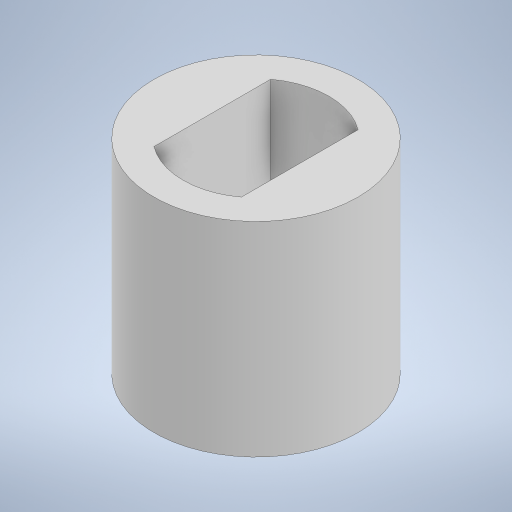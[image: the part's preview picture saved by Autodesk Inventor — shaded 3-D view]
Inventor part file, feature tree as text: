
AUTODESK INVENTOR PART (.ipt)
format: ipt  version: 2023 (Build 270158000, 158)  size: 248,320 bytes
history: native  units: in
note: dims shown in document units (in); Inventor stores cm internally (conversion verified against a paired STEP export)
features: extrude x2, sketch x2
ambient origin geometry x8: Origin, YZ Plane, XZ Plane, XY Plane, X Axis, Y Axis, Z Axis, Center Point
bodies: Solid1 (feature_tree)
feature tree (4):
  extrude  "Extrusion1"  Depth=0.2756in TaperAngle=0.0deg
  extrude  "Extrusion2"  Depth=0.1181in
  sketch  "Sketch1"  dims[d0=0.2756in d1=0.2756in d2=0.0in]
  sketch  "Sketch2"  dims[d3=0.1969in d4=0.1181in d5=0.2165in d6=0.2362in d7=0.0in]
